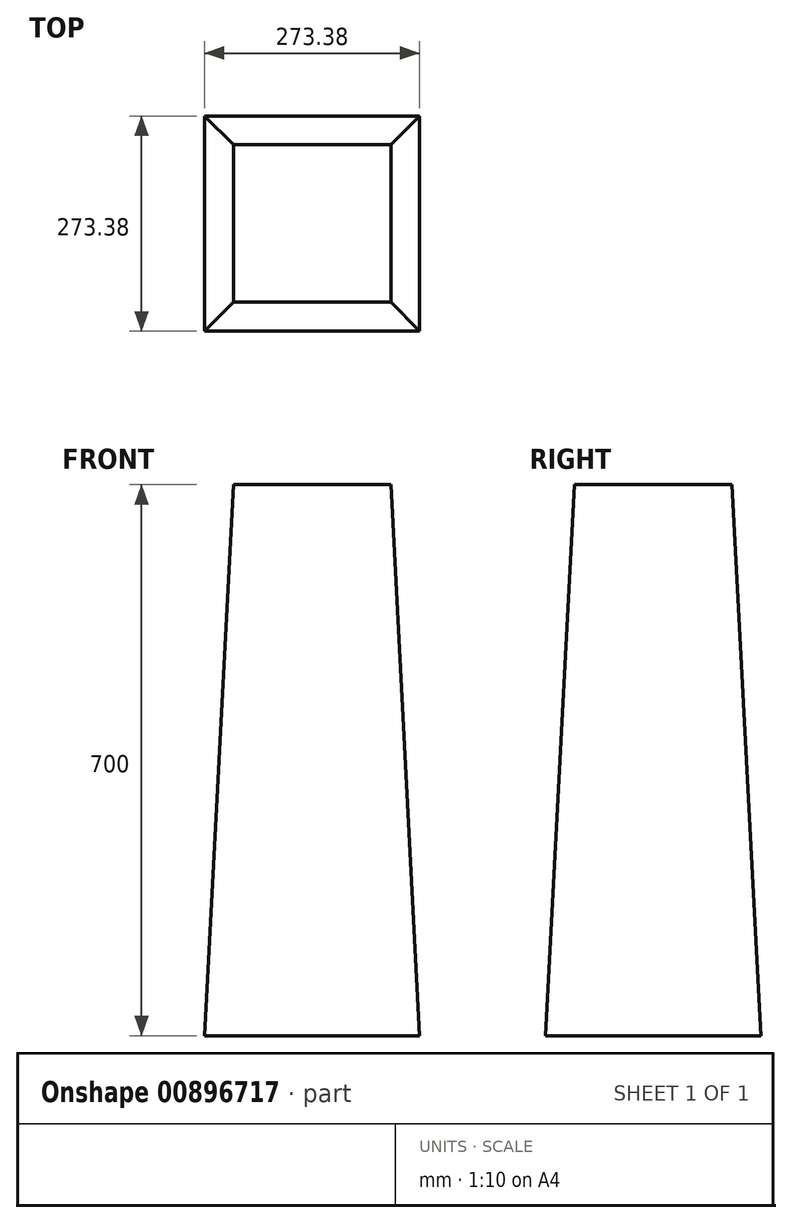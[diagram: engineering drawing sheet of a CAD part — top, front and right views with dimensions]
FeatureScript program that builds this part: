
annotation { "Feature Type Name" : "Feature", "Feature Type Description" : "" }
export const myFeature = defineFeature(function(context is Context, id is Id, definition is map)
    precondition{}
    {
        {
            var Q0;
            Q0=qCreatedBy(makeId("Top.planeOp"),FACE);
            var sketch = newSketch(context, id + "F0", { "sketchPlane" : qUnion([Q0])});
            skLineSegment(sketch, "E0.bottom", {"start": v(-100, 100) * mm, "end": v(100, 100) * mm});
            skLineSegment(sketch, "E0.top", {"start": v(-100, -100) * mm, "end": v(100, -100) * mm});
            skLineSegment(sketch, "E0.left", {"start": v(-100, 100) * mm, "end": v(-100, -100) * mm});
            skLineSegment(sketch, "E0.right", {"start": v(100, 100) * mm, "end": v(100, -100) * mm});
            skLineSegment(sketch, "E1", {"start": v(-100, 100) * mm, "end": v(100, -100) * mm, "construction": true});
            skSolve(sketch);
        }
        {
            var Q0;
            Q0 = qSketchRegion(id + "F0", true);
            extrude(context, id + "F1", {"entities" : qUnion([Q0]), "oppositeDirection" : true, "depth" : 700 * mm, "offsetDistance" : 25.4 * mm, "hasDraft" : true, "draftAngle" : 3 * degree});
        }
    });
